# Revit family: PKFY-P25VLM-E(ET)
name_source: partatom
category: Mechanical Equipment
revit_build: Autodesk Revit 2016 (Build: 20150220_1215(x64)
units: mm (PartAtom-declared; Revit-internal decimal feet)

## family parameters
Always vertical = Yes
Cut with Voids When Loaded = No
Host = Wall
OmniClass Number = 23.75.00.00
OmniClass Title = Climate Control (HVAC)
Part Type = Normal
Room Calculation Point = No
Round Connector Dimension = Use Radius
Shared = No

## types (5) — shared parameters
Air fitter = PP Honeycomb
Connectable outdoor unit = CITY MULTI
Cooling Current Input (A) = 0 A
Cooling Power Input (kW) = 0.03
Cooling capacity (kW) = 2.8
Depth (mm) = 237 mm  [stored 0.777559 ft]
Drain pipe_radius (mm) = 8 mm  [stored 0.0262467 ft]
External Finish = Plastic
Fan Air flow rate (Low-Mid2-Mid1-High) (m3/min) = 4.0 -4.6 -5.4 -6.7
Fan Driving mechanism = Direct driven
Fan External static press (Pa(mmH2O)) = 0 (0)
Fan Motor Output (kW) = 0.03
Fan Quantity = 1
Fan Type = Line flow fan
Fan motor type = DC motor
Gas pipe_radius (mm) = 6.35 mm  [stored 0.0208333 ft]
Heat exchanger = Cross fin (Aluminum fin and copper tube)
Heating Current Input (A) = 0 A
Heating Power Input (kW) = 0.02
Heating capacity (kW) = 3.2
Height (mm) = 299 mm  [stored 0.980971 ft]
Insulation material = Polyethylene sheet
Liquid pipe_radius (mm) = 3.175 mm  [stored 0.0104167 ft]
Manufacturer = Mitsubishi Electric Corporation
Model = PKFY-P25VLM-E(ET)
Noise level (Low-Mid2-Mid1-High) (dB<A>) = 22 - 27 - 31 - 35 (measured in anechoic room)
Outdoor unit refrigerant type = R410A
Phase = 1
Protection Device = Fuse
Refrigerant control device = LEV
Space View = Yes
Subcategory = HVAC
URL = http://www.mitsubishielectric.com
Unit Weight (kg) = 11.00 kg
Width (mm) = 773 mm  [stored 2.53609 ft]

## per-type parameters (varying)
| type | Hertz | Voltage |
| PKFY-P25VLM-E(ET)_220V50Hz | 50 Hz | 220 V |
| PKFY-P25VLM-E(ET)_230V50Hz | 50 Hz | 230 V |
| PKFY-P25VLM-E(ET)_240V50Hz | 50 Hz | 240 V |
| PKFY-P25VLM-E(ET)_220V60Hz | 60 Hz | 220 V |
| PKFY-P25VLM-E(ET)_230V60Hz | 60 Hz | 220 V |

note: [stored X ft] marks values corroborated as IEEE doubles in the binary element streams (Revit-internal decimal feet)

## geometry (parser evidence)
native form markers: Sweep x2
no freeform markers — native parametric forms only
